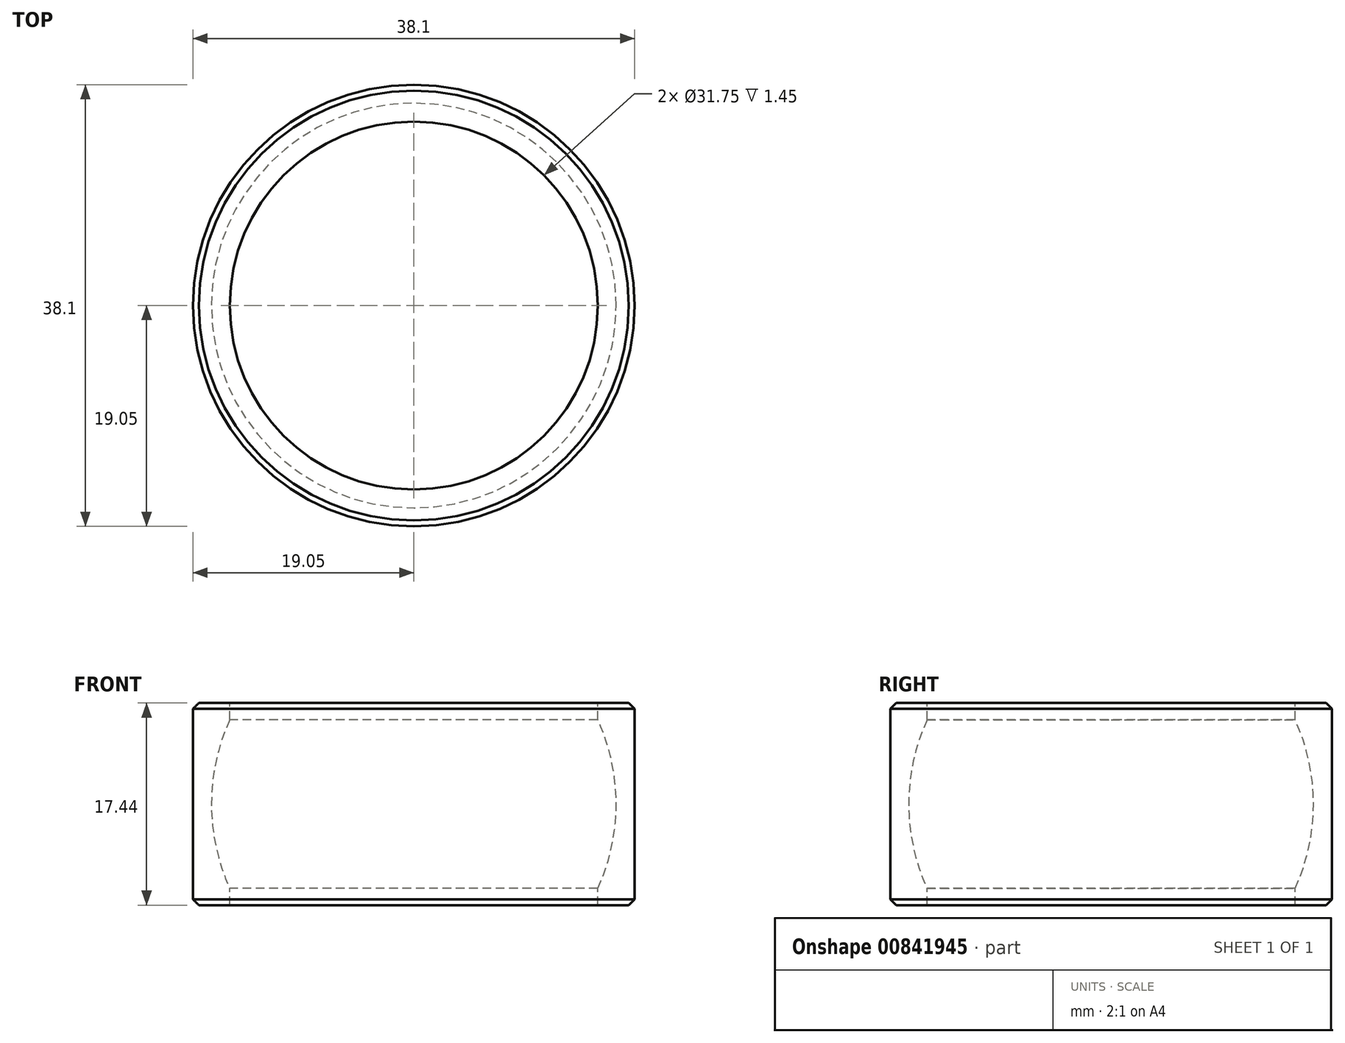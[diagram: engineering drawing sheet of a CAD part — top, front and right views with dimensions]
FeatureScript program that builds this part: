
annotation { "Feature Type Name" : "Feature", "Feature Type Description" : "" }
export const myFeature = defineFeature(function(context is Context, id is Id, definition is map)
    precondition{}
    {
        {
            var Q0;
            Q0=qCreatedBy(makeId("Front.planeOp"),FACE);
            var sketch = newSketch(context, id + "F0", { "sketchPlane" : qUnion([Q0])});
            skLineSegment(sketch, "E0", {"start": v(-19.05, -8.72) * mm, "end": v(-19.05, 8.72) * mm});
            skLineSegment(sketch, "E1", {"start": v(-19.05, 8.72) * mm, "end": v(-15.88, 8.72) * mm});
            skLineSegment(sketch, "E2", {"start": v(-15.88, 8.72) * mm, "end": v(-15.88, 7.27) * mm});
            skArc(sketch, "E3", {"start": v(-15.88, 7.27) * mm, "mid": v(-17.46, 0) * mm, "end": v(-15.88, -7.27) * mm});
            skLineSegment(sketch, "E4", {"start": v(-19.05, -8.72) * mm, "end": v(-15.88, -8.72) * mm});
            skLineSegment(sketch, "E5", {"start": v(-15.88, -8.72) * mm, "end": v(-15.88, -7.27) * mm});
            skLineSegment(sketch, "E6", {"start": v(0, 8.54) * mm, "end": v(0, -10.04) * mm, "construction": true});
            skSolve(sketch);
        }
        {
            var Q0;
            Q0=qSketchRegion(id+"F0",true);
            var Q1;
            Q1=sQuery(id+"F0.wireOp",EDGE,"E6");
            revolve(context, id + "F1", {"surfaceOperationType" : NewSurfaceOperationType.NEW, "entities" : qUnion([Q0]), "axis" : qUnion([Q1]), "revolveType" : RevolveType.FULL});
        }
        {
            var Q0;
            Q0=makeQuery(id+"F1.opRevolve","SWEPT_EDGE",EDGE,{"disambiguationData":[OSD([sQuery(id+"F0.wireOp",EDGE,"E0"),sQuery(id+"F0.wireOp",EDGE,"E1")])]});
            var Q1;
            Q1=makeQuery(id+"F1.opRevolve","SWEPT_EDGE",EDGE,{"disambiguationData":[OSD([sQuery(id+"F0.wireOp",EDGE,"E0"),sQuery(id+"F0.wireOp",EDGE,"E4")])]});
            chamfer(context, id + "F2", {"entities" : qUnion([Q0, Q1]), "width" : 0.5 * mm, "tangentPropagation" : true});
        }
    });
